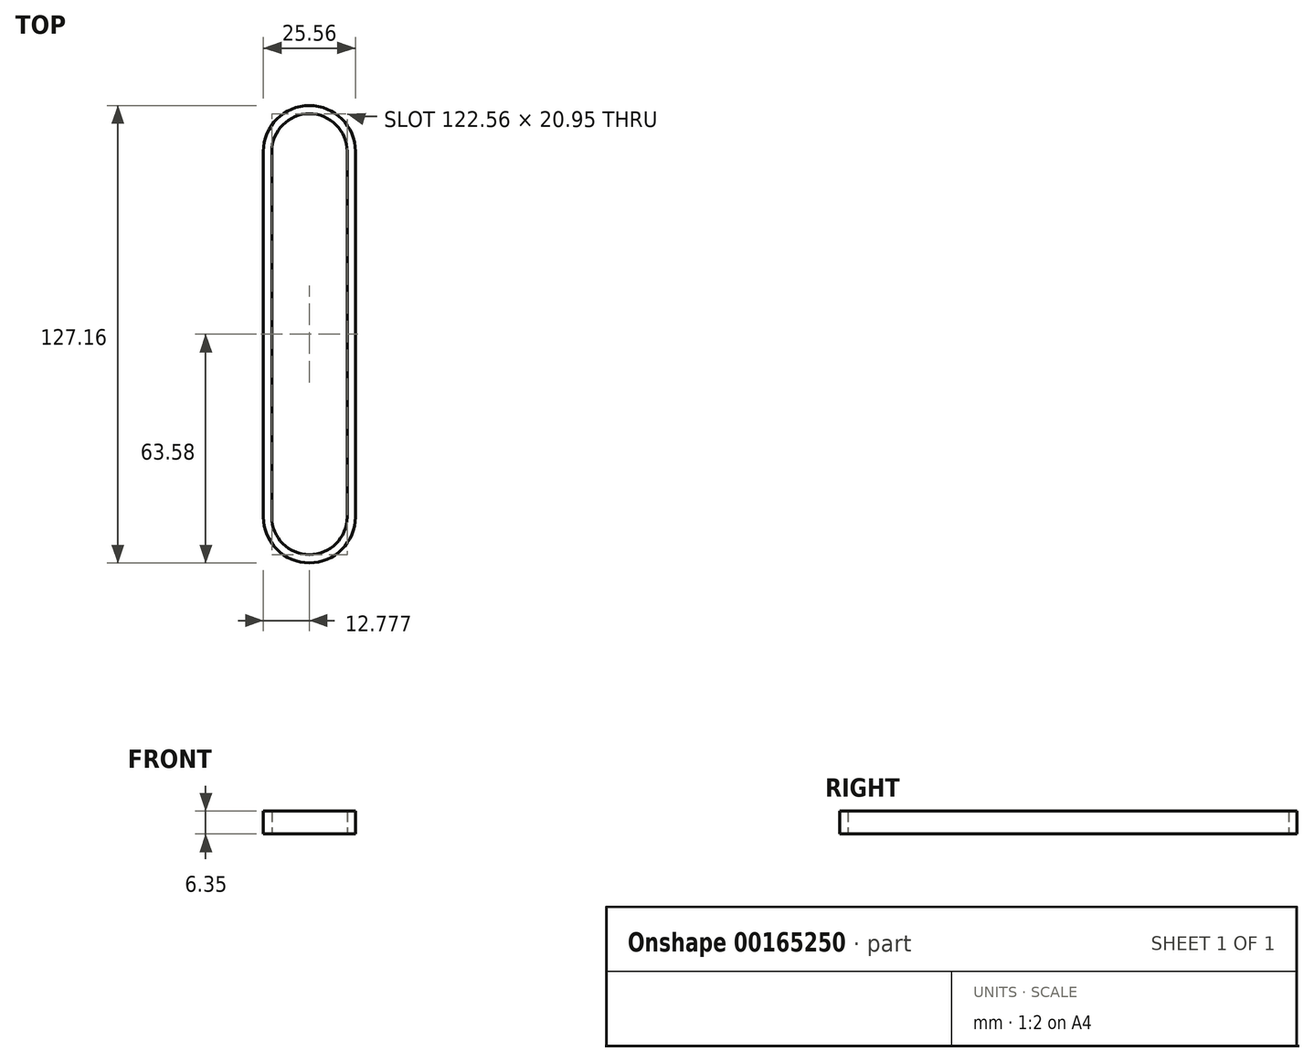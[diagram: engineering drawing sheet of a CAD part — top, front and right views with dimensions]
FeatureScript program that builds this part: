
annotation { "Feature Type Name" : "Feature", "Feature Type Description" : "" }
export const myFeature = defineFeature(function(context is Context, id is Id, definition is map)
    precondition{}
    {
        {
            var Q0;
            Q0=qCreatedBy(makeId("Top.planeOp"),FACE);
            var sketch = newSketch(context, id + "F0", { "sketchPlane" : qUnion([Q0])});
            skLineSegment(sketch, "E0.bottom", {"start": v(0, 0) * mm, "end": v(20.96, 0) * mm, "construction": true});
            skLineSegment(sketch, "E0.top", {"start": v(0, 101.6) * mm, "end": v(20.96, 101.6) * mm, "construction": true});
            skLineSegment(sketch, "E0.left", {"start": v(0, 0) * mm, "end": v(0, 101.6) * mm});
            skLineSegment(sketch, "E0.right", {"start": v(20.96, 0) * mm, "end": v(20.96, 101.6) * mm});
            skArc(sketch, "E1", {"start": v(20.96, 101.6) * mm, "mid": v(10.48, 112.08) * mm, "end": v(0, 101.6) * mm});
            skArc(sketch, "E2", {"start": v(0, 0) * mm, "mid": v(10.48, -10.48) * mm, "end": v(20.96, 0) * mm});
            skLineSegment(sketch, "E3", {"start": v(0, 101.6) * mm, "end": v(-2.3, 101.6) * mm, "construction": true});
            skLineSegment(sketch, "E4", {"start": v(20.96, 101.6) * mm, "end": v(23.25, 101.6) * mm, "construction": true});
            skLineSegment(sketch, "E5", {"start": v(23.26, 101.6) * mm, "end": v(23.26, 0) * mm});
            skLineSegment(sketch, "E6", {"start": v(23.25, 0) * mm, "end": v(20.96, 0) * mm, "construction": true});
            skLineSegment(sketch, "E7", {"start": v(0, 0) * mm, "end": v(-2.3, 0) * mm});
            skLineSegment(sketch, "E8", {"start": v(-2.3, 0) * mm, "end": v(-2.3, 101.6) * mm});
            skArc(sketch, "E9", {"start": v(-2.3, 0) * mm, "mid": v(10.48, -12.78) * mm, "end": v(23.26, 0) * mm});
            skArc(sketch, "E10", {"start": v(23.25, 101.6) * mm, "mid": v(10.48, 114.38) * mm, "end": v(-2.3, 101.6) * mm});
            skSolve(sketch);
        }
        {
            var Q0;
            Q0=qSketchRegion(id+"F0",true);
            extrude(context, id + "F1", {"entities" : qUnion([Q0]), "depth" : 6.35 * mm});
        }
    });
